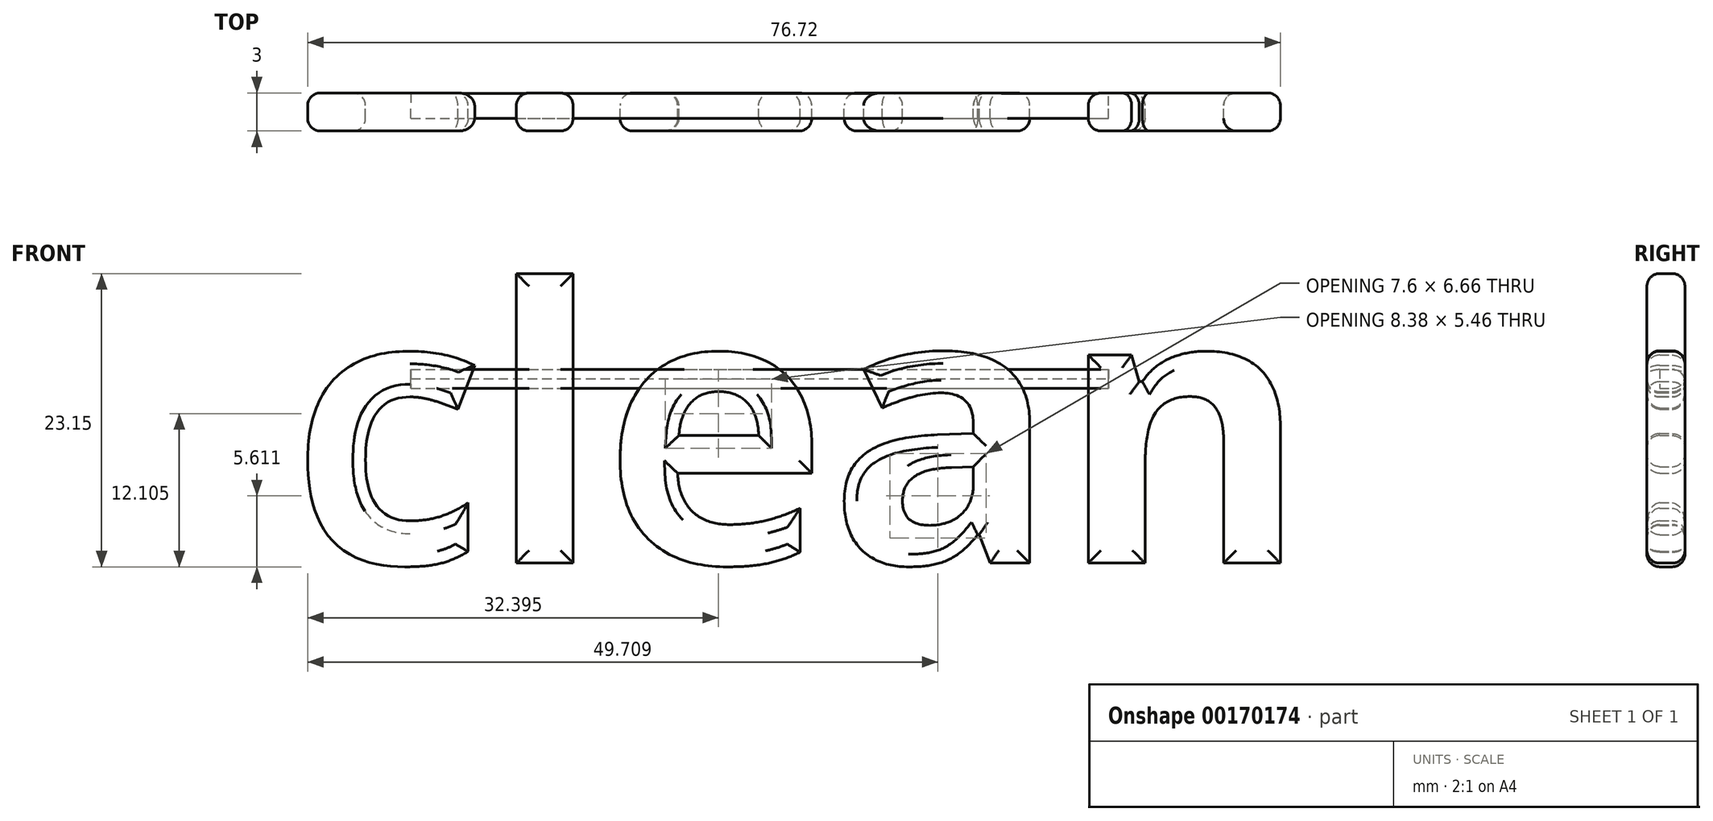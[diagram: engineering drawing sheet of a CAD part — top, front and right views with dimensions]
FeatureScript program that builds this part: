
annotation { "Feature Type Name" : "Feature", "Feature Type Description" : "" }
export const myFeature = defineFeature(function(context is Context, id is Id, definition is map)
    precondition{}
    {
        {
            var Q0;
            Q0=qCreatedBy(makeId("Front.planeOp"),FACE);
            var sketch = newSketch(context, id + "F0", { "sketchPlane" : qUnion([Q0])});
            skText(sketch, "E0", { "text": "clean", "fontName": "OpenSans-Bold.ttf"});
            const initialGuessF0  = {"E0": [0, 0, 1, 0, 0.02165]};
            skSetInitialGuess(sketch, initialGuessF0);
            skSolve(sketch);
        }
        {
            var Q0;
            Q0=qSketchRegion(id+"F0",true);
            extrude(context, id + "F1", {"entities" : qUnion([Q0]), "depth" : 3 * mm});
        }
        {
            var Q0;
            Q0=qCreatedBy(makeId("Front.planeOp"),FACE);
            var sketch = newSketch(context, id + "F2", { "sketchPlane" : qUnion([Q0])});
            skLineSegment(sketch, "E1.bottom", {"start": v(9.5, 15.3) * mm, "end": v(64.5, 15.3) * mm});
            skLineSegment(sketch, "E1.top", {"start": v(9.5, 13.8) * mm, "end": v(64.5, 13.8) * mm});
            skLineSegment(sketch, "E1.left", {"start": v(9.5, 15.3) * mm, "end": v(9.5, 13.8) * mm});
            skLineSegment(sketch, "E1.right", {"start": v(64.5, 15.3) * mm, "end": v(64.5, 13.8) * mm});
            skSolve(sketch);
        }
        {
            var Q0;
            Q0=makeQuery(id+"F2.imprint","IMPRINT",FACE,{"disambiguationData":[TD([[makeQuery(id+"F2.imprint","IMPRINT",EDGE,{"derivedFrom":sQuery(id+"F2.wireOp",EDGE,"E1.bottom")}),-1.0]])]});
            extrude(context, id + "F3", {"entities" : qUnion([Q0]), "depth" : 2 * mm});
        }
        {
            var Q0;
            Q0=makeQuery(id+"F1.opExtrude","CAP_FACE",FACE,{"disambiguationData":[OSD([sQuery(id+"F0.wireOp",EDGE,"E0.sketch_text.stroke-63"),sQuery(id+"F0.wireOp",EDGE,"E0.sketch_text.stroke-64"),sQuery(id+"F0.wireOp",EDGE,"E0.sketch_text.stroke-65"),sQuery(id+"F0.wireOp",EDGE,"E0.sketch_text.stroke-66"),sQuery(id+"F0.wireOp",EDGE,"E0.sketch_text.stroke-67"),sQuery(id+"F0.wireOp",EDGE,"E0.sketch_text.stroke-68"),sQuery(id+"F0.wireOp",EDGE,"E0.sketch_text.stroke-69"),sQuery(id+"F0.wireOp",EDGE,"E0.sketch_text.stroke-70"),sQuery(id+"F0.wireOp",EDGE,"E0.sketch_text.stroke-71"),sQuery(id+"F0.wireOp",EDGE,"E0.sketch_text.stroke-72"),sQuery(id+"F0.wireOp",EDGE,"E0.sketch_text.stroke-73"),sQuery(id+"F0.wireOp",EDGE,"E0.sketch_text.stroke-74"),sQuery(id+"F0.wireOp",EDGE,"E0.sketch_text.stroke-75"),sQuery(id+"F0.wireOp",EDGE,"E0.sketch_text.stroke-76"),sQuery(id+"F0.wireOp",EDGE,"E0.sketch_text.stroke-77"),sQuery(id+"F0.wireOp",EDGE,"E0.sketch_text.stroke-78"),sQuery(id+"F0.wireOp",EDGE,"E0.sketch_text.stroke-79")])],"isStart":true});
            var Q1;
            Q1=makeQuery(id+"F1.opExtrude","CAP_FACE",FACE,{"disambiguationData":[OSD([sQuery(id+"F0.wireOp",EDGE,"E0.sketch_text.stroke-38"),sQuery(id+"F0.wireOp",EDGE,"E0.sketch_text.stroke-39"),sQuery(id+"F0.wireOp",EDGE,"E0.sketch_text.stroke-40"),sQuery(id+"F0.wireOp",EDGE,"E0.sketch_text.stroke-41"),sQuery(id+"F0.wireOp",EDGE,"E0.sketch_text.stroke-42"),sQuery(id+"F0.wireOp",EDGE,"E0.sketch_text.stroke-43"),sQuery(id+"F0.wireOp",EDGE,"E0.sketch_text.stroke-44"),sQuery(id+"F0.wireOp",EDGE,"E0.sketch_text.stroke-45"),sQuery(id+"F0.wireOp",EDGE,"E0.sketch_text.stroke-46"),sQuery(id+"F0.wireOp",EDGE,"E0.sketch_text.stroke-47"),sQuery(id+"F0.wireOp",EDGE,"E0.sketch_text.stroke-48"),sQuery(id+"F0.wireOp",EDGE,"E0.sketch_text.stroke-49"),sQuery(id+"F0.wireOp",EDGE,"E0.sketch_text.stroke-50"),sQuery(id+"F0.wireOp",EDGE,"E0.sketch_text.stroke-51"),sQuery(id+"F0.wireOp",EDGE,"E0.sketch_text.stroke-52"),sQuery(id+"F0.wireOp",EDGE,"E0.sketch_text.stroke-53"),sQuery(id+"F0.wireOp",EDGE,"E0.sketch_text.stroke-54"),sQuery(id+"F0.wireOp",EDGE,"E0.sketch_text.stroke-55"),sQuery(id+"F0.wireOp",EDGE,"E0.sketch_text.stroke-56"),sQuery(id+"F0.wireOp",EDGE,"E0.sketch_text.stroke-57"),sQuery(id+"F0.wireOp",EDGE,"E0.sketch_text.stroke-58"),sQuery(id+"F0.wireOp",EDGE,"E0.sketch_text.stroke-59"),sQuery(id+"F0.wireOp",EDGE,"E0.sketch_text.stroke-60"),sQuery(id+"F0.wireOp",EDGE,"E0.sketch_text.stroke-61"),sQuery(id+"F0.wireOp",EDGE,"E0.sketch_text.stroke-62")])],"isStart":true});
            var Q2;
            Q2=makeQuery(id+"F1.opExtrude","CAP_FACE",FACE,{"disambiguationData":[OSD([sQuery(id+"F0.wireOp",EDGE,"E0.sketch_text.stroke-18"),sQuery(id+"F0.wireOp",EDGE,"E0.sketch_text.stroke-19"),sQuery(id+"F0.wireOp",EDGE,"E0.sketch_text.stroke-20"),sQuery(id+"F0.wireOp",EDGE,"E0.sketch_text.stroke-21"),sQuery(id+"F0.wireOp",EDGE,"E0.sketch_text.stroke-22"),sQuery(id+"F0.wireOp",EDGE,"E0.sketch_text.stroke-23"),sQuery(id+"F0.wireOp",EDGE,"E0.sketch_text.stroke-24"),sQuery(id+"F0.wireOp",EDGE,"E0.sketch_text.stroke-25"),sQuery(id+"F0.wireOp",EDGE,"E0.sketch_text.stroke-26"),sQuery(id+"F0.wireOp",EDGE,"E0.sketch_text.stroke-27"),sQuery(id+"F0.wireOp",EDGE,"E0.sketch_text.stroke-28"),sQuery(id+"F0.wireOp",EDGE,"E0.sketch_text.stroke-29"),sQuery(id+"F0.wireOp",EDGE,"E0.sketch_text.stroke-30"),sQuery(id+"F0.wireOp",EDGE,"E0.sketch_text.stroke-31"),sQuery(id+"F0.wireOp",EDGE,"E0.sketch_text.stroke-32"),sQuery(id+"F0.wireOp",EDGE,"E0.sketch_text.stroke-33"),sQuery(id+"F0.wireOp",EDGE,"E0.sketch_text.stroke-34"),sQuery(id+"F0.wireOp",EDGE,"E0.sketch_text.stroke-35"),sQuery(id+"F0.wireOp",EDGE,"E0.sketch_text.stroke-36"),sQuery(id+"F0.wireOp",EDGE,"E0.sketch_text.stroke-37")])],"isStart":true});
            var Q3;
            Q3=makeQuery(id+"F1.opExtrude","CAP_FACE",FACE,{"disambiguationData":[OSD([sQuery(id+"F0.wireOp",EDGE,"E0.sketch_text.stroke-14"),sQuery(id+"F0.wireOp",EDGE,"E0.sketch_text.stroke-15"),sQuery(id+"F0.wireOp",EDGE,"E0.sketch_text.stroke-16"),sQuery(id+"F0.wireOp",EDGE,"E0.sketch_text.stroke-17")])],"isStart":true});
            var Q4;
            Q4=makeQuery(id+"F1.opExtrude","CAP_FACE",FACE,{"disambiguationData":[OSD([sQuery(id+"F0.wireOp",EDGE,"E0.sketch_text.stroke-0"),sQuery(id+"F0.wireOp",EDGE,"E0.sketch_text.stroke-1"),sQuery(id+"F0.wireOp",EDGE,"E0.sketch_text.stroke-2"),sQuery(id+"F0.wireOp",EDGE,"E0.sketch_text.stroke-3"),sQuery(id+"F0.wireOp",EDGE,"E0.sketch_text.stroke-4"),sQuery(id+"F0.wireOp",EDGE,"E0.sketch_text.stroke-5"),sQuery(id+"F0.wireOp",EDGE,"E0.sketch_text.stroke-6"),sQuery(id+"F0.wireOp",EDGE,"E0.sketch_text.stroke-7"),sQuery(id+"F0.wireOp",EDGE,"E0.sketch_text.stroke-8"),sQuery(id+"F0.wireOp",EDGE,"E0.sketch_text.stroke-9"),sQuery(id+"F0.wireOp",EDGE,"E0.sketch_text.stroke-10"),sQuery(id+"F0.wireOp",EDGE,"E0.sketch_text.stroke-11"),sQuery(id+"F0.wireOp",EDGE,"E0.sketch_text.stroke-12"),sQuery(id+"F0.wireOp",EDGE,"E0.sketch_text.stroke-13")])],"isStart":true});
            var Q5;
            Q5=makeQuery(id+"F3.opExtrude","CAP_EDGE",EDGE,{"disambiguationData":[OSD([sQuery(id+"F2.wireOp",EDGE,"E1.top")])],"isStart":true});
            var Q6;
            Q6=makeQuery(id+"F3.opExtrude","CAP_EDGE",EDGE,{"disambiguationData":[OSD([sQuery(id+"F2.wireOp",EDGE,"E1.bottom")])],"isStart":true});
            var Q7;
            Q7=makeQuery(id+"F1.opExtrude","CAP_FACE",FACE,{"disambiguationData":[OSD([sQuery(id+"F0.wireOp",EDGE,"E0.sketch_text.stroke-63"),sQuery(id+"F0.wireOp",EDGE,"E0.sketch_text.stroke-64"),sQuery(id+"F0.wireOp",EDGE,"E0.sketch_text.stroke-65"),sQuery(id+"F0.wireOp",EDGE,"E0.sketch_text.stroke-66"),sQuery(id+"F0.wireOp",EDGE,"E0.sketch_text.stroke-67"),sQuery(id+"F0.wireOp",EDGE,"E0.sketch_text.stroke-68"),sQuery(id+"F0.wireOp",EDGE,"E0.sketch_text.stroke-69"),sQuery(id+"F0.wireOp",EDGE,"E0.sketch_text.stroke-70"),sQuery(id+"F0.wireOp",EDGE,"E0.sketch_text.stroke-71"),sQuery(id+"F0.wireOp",EDGE,"E0.sketch_text.stroke-72"),sQuery(id+"F0.wireOp",EDGE,"E0.sketch_text.stroke-73"),sQuery(id+"F0.wireOp",EDGE,"E0.sketch_text.stroke-74"),sQuery(id+"F0.wireOp",EDGE,"E0.sketch_text.stroke-75"),sQuery(id+"F0.wireOp",EDGE,"E0.sketch_text.stroke-76"),sQuery(id+"F0.wireOp",EDGE,"E0.sketch_text.stroke-77"),sQuery(id+"F0.wireOp",EDGE,"E0.sketch_text.stroke-78"),sQuery(id+"F0.wireOp",EDGE,"E0.sketch_text.stroke-79")])],"isStart":false});
            var Q8;
            Q8=makeQuery(id+"F1.opExtrude","CAP_FACE",FACE,{"disambiguationData":[OSD([sQuery(id+"F0.wireOp",EDGE,"E0.sketch_text.stroke-38"),sQuery(id+"F0.wireOp",EDGE,"E0.sketch_text.stroke-39"),sQuery(id+"F0.wireOp",EDGE,"E0.sketch_text.stroke-40"),sQuery(id+"F0.wireOp",EDGE,"E0.sketch_text.stroke-41"),sQuery(id+"F0.wireOp",EDGE,"E0.sketch_text.stroke-42"),sQuery(id+"F0.wireOp",EDGE,"E0.sketch_text.stroke-43"),sQuery(id+"F0.wireOp",EDGE,"E0.sketch_text.stroke-44"),sQuery(id+"F0.wireOp",EDGE,"E0.sketch_text.stroke-45"),sQuery(id+"F0.wireOp",EDGE,"E0.sketch_text.stroke-46"),sQuery(id+"F0.wireOp",EDGE,"E0.sketch_text.stroke-47"),sQuery(id+"F0.wireOp",EDGE,"E0.sketch_text.stroke-48"),sQuery(id+"F0.wireOp",EDGE,"E0.sketch_text.stroke-49"),sQuery(id+"F0.wireOp",EDGE,"E0.sketch_text.stroke-50"),sQuery(id+"F0.wireOp",EDGE,"E0.sketch_text.stroke-51"),sQuery(id+"F0.wireOp",EDGE,"E0.sketch_text.stroke-52"),sQuery(id+"F0.wireOp",EDGE,"E0.sketch_text.stroke-53"),sQuery(id+"F0.wireOp",EDGE,"E0.sketch_text.stroke-54"),sQuery(id+"F0.wireOp",EDGE,"E0.sketch_text.stroke-55"),sQuery(id+"F0.wireOp",EDGE,"E0.sketch_text.stroke-56"),sQuery(id+"F0.wireOp",EDGE,"E0.sketch_text.stroke-57"),sQuery(id+"F0.wireOp",EDGE,"E0.sketch_text.stroke-58"),sQuery(id+"F0.wireOp",EDGE,"E0.sketch_text.stroke-59"),sQuery(id+"F0.wireOp",EDGE,"E0.sketch_text.stroke-60"),sQuery(id+"F0.wireOp",EDGE,"E0.sketch_text.stroke-61"),sQuery(id+"F0.wireOp",EDGE,"E0.sketch_text.stroke-62")])],"isStart":false});
            var Q9;
            Q9=makeQuery(id+"F1.opExtrude","CAP_FACE",FACE,{"disambiguationData":[OSD([sQuery(id+"F0.wireOp",EDGE,"E0.sketch_text.stroke-18"),sQuery(id+"F0.wireOp",EDGE,"E0.sketch_text.stroke-19"),sQuery(id+"F0.wireOp",EDGE,"E0.sketch_text.stroke-20"),sQuery(id+"F0.wireOp",EDGE,"E0.sketch_text.stroke-21"),sQuery(id+"F0.wireOp",EDGE,"E0.sketch_text.stroke-22"),sQuery(id+"F0.wireOp",EDGE,"E0.sketch_text.stroke-23"),sQuery(id+"F0.wireOp",EDGE,"E0.sketch_text.stroke-24"),sQuery(id+"F0.wireOp",EDGE,"E0.sketch_text.stroke-25"),sQuery(id+"F0.wireOp",EDGE,"E0.sketch_text.stroke-26"),sQuery(id+"F0.wireOp",EDGE,"E0.sketch_text.stroke-27"),sQuery(id+"F0.wireOp",EDGE,"E0.sketch_text.stroke-28"),sQuery(id+"F0.wireOp",EDGE,"E0.sketch_text.stroke-29"),sQuery(id+"F0.wireOp",EDGE,"E0.sketch_text.stroke-30"),sQuery(id+"F0.wireOp",EDGE,"E0.sketch_text.stroke-31"),sQuery(id+"F0.wireOp",EDGE,"E0.sketch_text.stroke-32"),sQuery(id+"F0.wireOp",EDGE,"E0.sketch_text.stroke-33"),sQuery(id+"F0.wireOp",EDGE,"E0.sketch_text.stroke-34"),sQuery(id+"F0.wireOp",EDGE,"E0.sketch_text.stroke-35"),sQuery(id+"F0.wireOp",EDGE,"E0.sketch_text.stroke-36"),sQuery(id+"F0.wireOp",EDGE,"E0.sketch_text.stroke-37")])],"isStart":false});
            var Q10;
            Q10=makeQuery(id+"F1.opExtrude","CAP_FACE",FACE,{"disambiguationData":[OSD([sQuery(id+"F0.wireOp",EDGE,"E0.sketch_text.stroke-14"),sQuery(id+"F0.wireOp",EDGE,"E0.sketch_text.stroke-15"),sQuery(id+"F0.wireOp",EDGE,"E0.sketch_text.stroke-16"),sQuery(id+"F0.wireOp",EDGE,"E0.sketch_text.stroke-17")])],"isStart":false});
            var Q11;
            Q11=makeQuery(id+"F1.opExtrude","CAP_FACE",FACE,{"disambiguationData":[OSD([sQuery(id+"F0.wireOp",EDGE,"E0.sketch_text.stroke-0"),sQuery(id+"F0.wireOp",EDGE,"E0.sketch_text.stroke-1"),sQuery(id+"F0.wireOp",EDGE,"E0.sketch_text.stroke-2"),sQuery(id+"F0.wireOp",EDGE,"E0.sketch_text.stroke-3"),sQuery(id+"F0.wireOp",EDGE,"E0.sketch_text.stroke-4"),sQuery(id+"F0.wireOp",EDGE,"E0.sketch_text.stroke-5"),sQuery(id+"F0.wireOp",EDGE,"E0.sketch_text.stroke-6"),sQuery(id+"F0.wireOp",EDGE,"E0.sketch_text.stroke-7"),sQuery(id+"F0.wireOp",EDGE,"E0.sketch_text.stroke-8"),sQuery(id+"F0.wireOp",EDGE,"E0.sketch_text.stroke-9"),sQuery(id+"F0.wireOp",EDGE,"E0.sketch_text.stroke-10"),sQuery(id+"F0.wireOp",EDGE,"E0.sketch_text.stroke-11"),sQuery(id+"F0.wireOp",EDGE,"E0.sketch_text.stroke-12"),sQuery(id+"F0.wireOp",EDGE,"E0.sketch_text.stroke-13")])],"isStart":false});
            fillet(context, id + "F4", {"entities" : qUnion([Q0, Q1, Q2, Q3, Q4, Q5, Q6, Q7, Q8, Q9, Q10, Q11]), "radius" : 1 * mm, "tangentPropagation" : true, "allowEdgeOverflow" : false});
        }
    });
